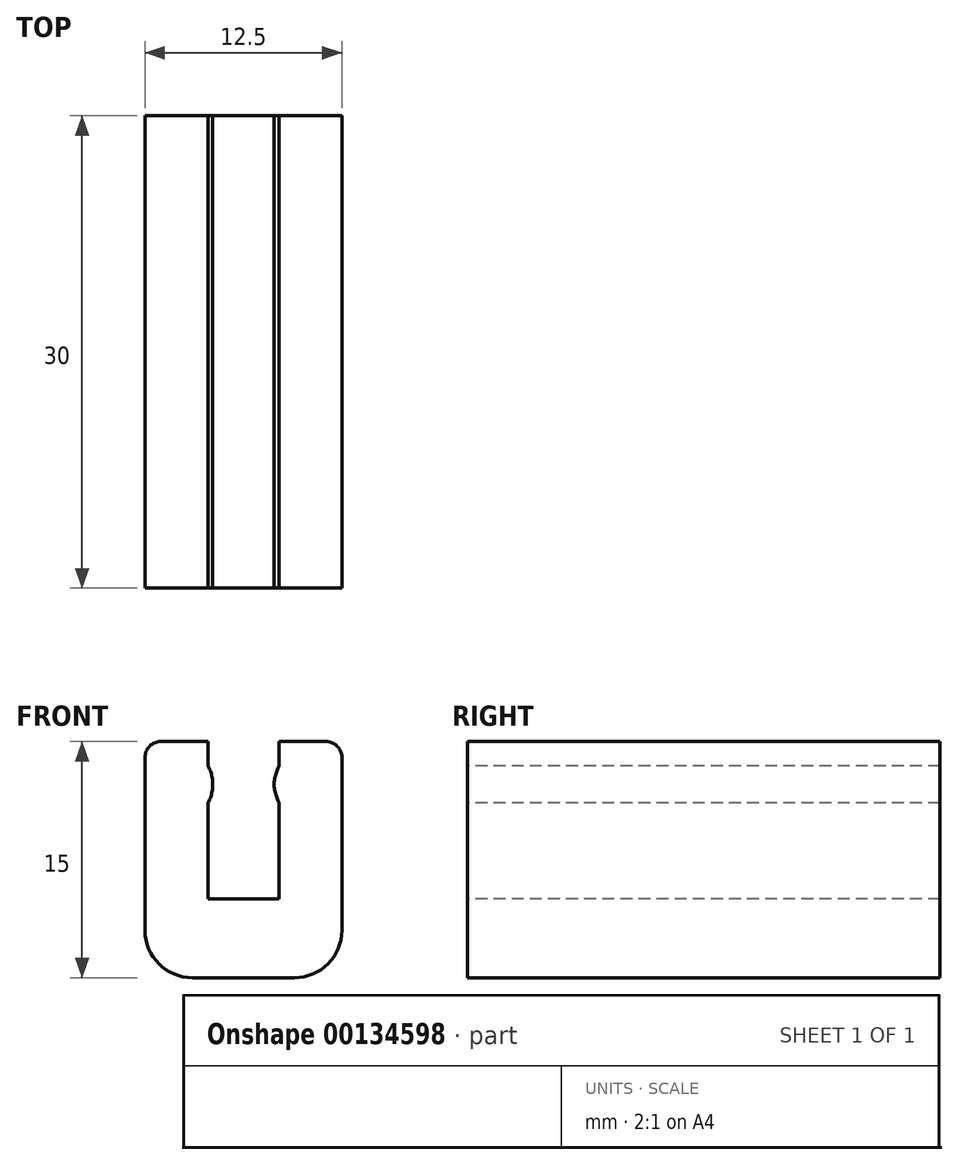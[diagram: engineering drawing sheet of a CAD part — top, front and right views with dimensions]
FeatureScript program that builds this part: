
annotation { "Feature Type Name" : "Feature", "Feature Type Description" : "" }
export const myFeature = defineFeature(function(context is Context, id is Id, definition is map)
    precondition{}
    {
        {
            var Q0;
            Q0=qCreatedBy(makeId("Top.planeOp"),FACE);
            var sketch = newSketch(context, id + "F0", { "sketchPlane" : qUnion([Q0])});
            skLineSegment(sketch, "E0.bottom", {"start": v(-7.04, 6.46) * mm, "end": v(-2.54, 6.46) * mm});
            skLineSegment(sketch, "E0.top", {"start": v(-7.04, -23.54) * mm, "end": v(-2.54, -23.54) * mm});
            skLineSegment(sketch, "E0.left", {"start": v(-7.04, 6.46) * mm, "end": v(-7.04, -23.54) * mm});
            skLineSegment(sketch, "E0.right", {"start": v(-2.54, 6.46) * mm, "end": v(-2.54, -23.54) * mm});
            skLineSegment(sketch, "E1.bottom", {"start": v(-7.04, 6.46) * mm, "end": v(-11.04, 6.46) * mm});
            skLineSegment(sketch, "E1.top", {"start": v(-7.04, -23.54) * mm, "end": v(-11.04, -23.54) * mm});
            skLineSegment(sketch, "E1.right", {"start": v(-11.04, 6.46) * mm, "end": v(-11.04, -23.54) * mm});
            skLineSegment(sketch, "E2.bottom", {"start": v(-2.54, 6.46) * mm, "end": v(1.46, 6.46) * mm});
            skLineSegment(sketch, "E2.top", {"start": v(-2.54, -23.54) * mm, "end": v(1.46, -23.54) * mm});
            skLineSegment(sketch, "E2.right", {"start": v(1.46, 6.46) * mm, "end": v(1.46, -23.54) * mm});
            skSolve(sketch);
        }
        {
            var Q0;
            Q0 = qSketchRegion(id + "F0", true);
            extrude(context, id + "F1", {"entities" : qUnion([Q0]), "oppositeDirection" : true, "depth" : 5 * mm});
        }
        {
            var Q0;
            Q0=makeQuery(id+"F0.imprint","IMPRINT",FACE,{"disambiguationData":[TD([[makeQuery(id+"F0.imprint","IMPRINT",EDGE,{"derivedFrom":sQuery(id+"F0.wireOp",EDGE,"E1.bottom")}),1.0]])]});
            var Q1;
            Q1=makeQuery(id+"F0.imprint","IMPRINT",FACE,{"disambiguationData":[TD([[makeQuery(id+"F0.imprint","IMPRINT",EDGE,{"derivedFrom":sQuery(id+"F0.wireOp",EDGE,"E2.bottom")}),-1.0]])]});
            extrude(context, id + "F2", {"entities" : qUnion([Q0, Q1]), "operationType" : NewBodyOperationType.ADD, "depth" : 10 * mm});
        }
        {
            var Q0;
            Q0=makeQuery(id+"F1.opExtrude","CAP_EDGE",EDGE,{"disambiguationData":[OSD([sQuery(id+"F0.wireOp",EDGE,"E2.right")])],"isStart":false});
            var Q1;
            Q1=makeQuery(id+"F1.opExtrude","CAP_EDGE",EDGE,{"disambiguationData":[OSD([sQuery(id+"F0.wireOp",EDGE,"E1.right")])],"isStart":false});
            fillet(context, id + "F3", {"entities" : qUnion([Q0, Q1]), "radius" : 3 * mm, "tangentPropagation" : true, "allowEdgeOverflow" : false});
        }
        {
            var Q0;
            Q0=makeQuery(id+"F2.opExtrude","CAP_EDGE",EDGE,{"disambiguationData":[OSD([sQuery(id+"F0.wireOp",EDGE,"E0.left")])],"isStart":false});
            var Q1;
            Q1=makeQuery(id+"F2.opExtrude","CAP_EDGE",EDGE,{"disambiguationData":[OSD([sQuery(id+"F0.wireOp",EDGE,"E1.right")])],"isStart":false});
            var Q2;
            Q2=makeQuery(id+"F2.opExtrude","CAP_EDGE",EDGE,{"disambiguationData":[OSD([sQuery(id+"F0.wireOp",EDGE,"E2.right")])],"isStart":false});
            var Q3;
            Q3=makeQuery(id+"F2.opExtrude","CAP_EDGE",EDGE,{"disambiguationData":[OSD([sQuery(id+"F0.wireOp",EDGE,"E0.right")])],"isStart":false});
            fillet(context, id + "F4", {"entities" : qUnion([Q0, Q1, Q2, Q3]), "radius" : 1 * mm, "tangentPropagation" : true, "allowEdgeOverflow" : false});
        }
        {
            var Q0;
            {var subQ0=sQuery(id+"F0.wireOp",EDGE,"E2.top");var subQ1=sQuery(id+"F0.wireOp",EDGE,"E1.top");Q0=makeQuery(id+"F2.boolean.opBoolean","MERGE",FACE,{"derivedFrom":[makeQuery(id+"F1.opExtrude","SWEPT_FACE",FACE,{"disambiguationData":[OSD([sQuery(id+"F0.wireOp",EDGE,"E0.top"),subQ1,subQ0])]}),makeQuery(id+"F2.opExtrude","SWEPT_FACE",FACE,{"disambiguationData":[OSD([subQ1])]}),makeQuery(id+"F2.opExtrude","SWEPT_FACE",FACE,{"disambiguationData":[OSD([subQ0])]})]});}
            var sketch = newSketch(context, id + "F5", { "sketchPlane" : qUnion([Q0])});
            skFitSpline(sketch, "E3", {"points": [v(-2.54, 8.44) * mm, v(-2.84, 7.3) * mm, v(-2.54, 6.11) * mm], "startDerivative": vector(-1.08, -2.33) * mm, "endDerivative": vector(1.08, -2.33) * mm});
            skFitSpline(sketch, "E4", {"points": [v(-7.04, 8.44) * mm, v(-6.74, 7.3) * mm, v(-7.04, 6.11) * mm], "startDerivative": vector(1.28, -2.33) * mm, "endDerivative": vector(-1.28, -2.33) * mm});
            skSolve(sketch);
        }
        {
            var Q0;
            {var subQ0=sQuery(id+"F5.wireOp",EDGE,"E3");Q0=makeQuery(id+"F5.imprint","IMPRINT",FACE,{"disambiguationData":[TD([[makeQuery(id+"F5.imprint","IMPRINT",EDGE,{"derivedFrom":subQ0}),1.0]])]});}
            var Q1;
            {var subQ0=sQuery(id+"F5.wireOp",EDGE,"E4");Q1=makeQuery(id+"F5.imprint","IMPRINT",FACE,{"disambiguationData":[TD([[makeQuery(id+"F5.imprint","IMPRINT",EDGE,{"derivedFrom":subQ0}),-1.0]])]});}
            extrude(context, id + "F6", {"entities" : qUnion([Q0, Q1]), "operationType" : NewBodyOperationType.ADD, "oppositeDirection" : true, "depth" : 30 * mm});
        }
    });
